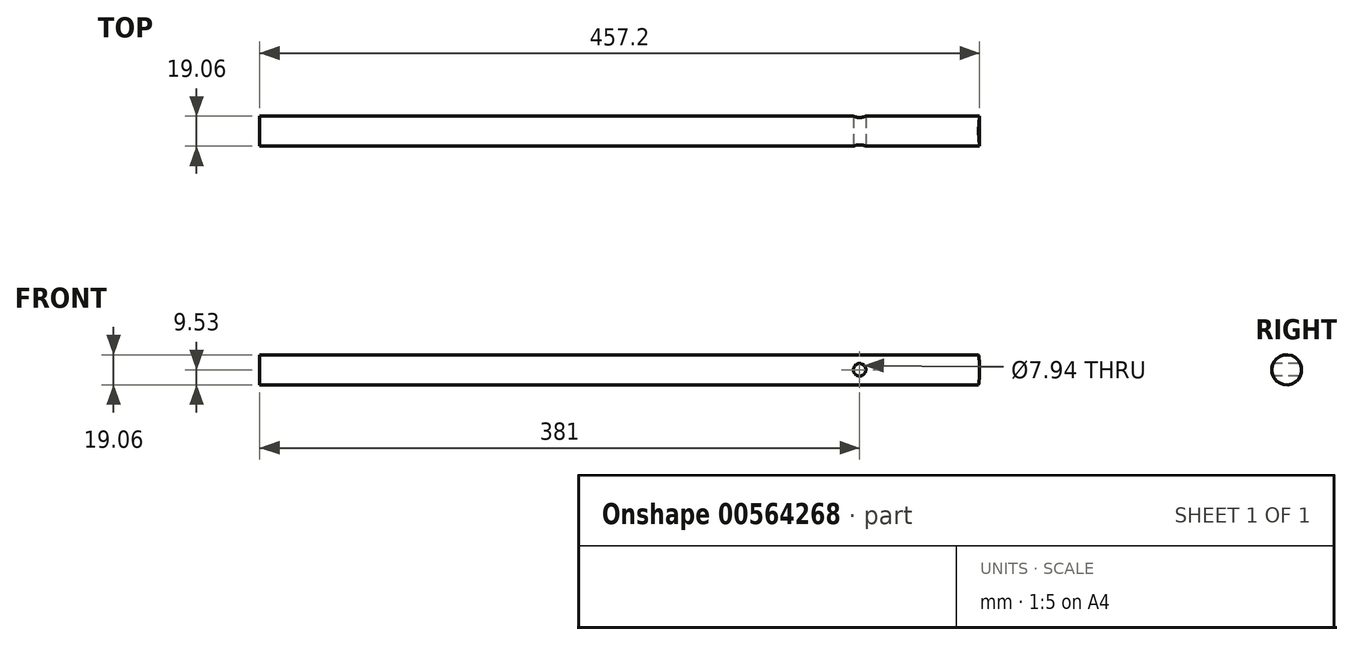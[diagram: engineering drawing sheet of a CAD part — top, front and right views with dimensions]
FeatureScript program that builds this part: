
annotation { "Feature Type Name" : "Feature", "Feature Type Description" : "" }
export const myFeature = defineFeature(function(context is Context, id is Id, definition is map)
    precondition{}
    {
        {
            var Q0;
            Q0=qCreatedBy(makeId("Right.planeOp"),FACE);
            var sketch = newSketch(context, id + "F0", { "sketchPlane" : qUnion([Q0])});
            skCircle(sketch, "E0", {"center": v(0, 0) * mm, "radius": 9.53 * mm});
            skSolve(sketch);
        }
        {
            var Q0;
            Q0=makeQuery(id+"F0.imprint","IMPRINT",FACE,{"disambiguationData":[TD([[makeQuery(id+"F0.imprint","IMPRINT",EDGE,{"derivedFrom":sQuery(id+"F0.wireOp",EDGE,"E0")}),1.0]])]});
            extrude(context, id + "F1", {"entities" : qUnion([Q0]), "endBound" : BoundingType.SYMMETRIC, "depth" : 457.2 * mm, "offsetDistance" : 25.4 * mm});
        }
        {
            var Q0;
            Q0=qCreatedBy(makeId("Front.planeOp"),FACE);
            var sketch = newSketch(context, id + "F2", { "sketchPlane" : qUnion([Q0])});
            skCircle(sketch, "E1", {"center": v(152.4, 0) * mm, "radius": 3.97 * mm});
            skArc(sketch, "E2", {"start": v(228, -9.52) * mm, "mid": v(228.6, 0) * mm, "end": v(228, 9.53) * mm});
            skLineSegment(sketch, "E3", {"start": v(228, 9.53) * mm, "end": v(235.25, 9.53) * mm});
            skLineSegment(sketch, "E4", {"start": v(235.25, 9.53) * mm, "end": v(235.25, -9.52) * mm});
            skLineSegment(sketch, "E5", {"start": v(235.25, -9.52) * mm, "end": v(228, -9.52) * mm});
            skSolve(sketch);
        }
        {
            var Q0;
            Q0 = qSketchRegion(id + "F2", true);
            extrude(context, id + "F3", {"entities" : qUnion([Q0]), "operationType" : NewBodyOperationType.REMOVE, "endBound" : BoundingType.SYMMETRIC, "oppositeDirection" : true, "depth" : 25.4 * mm, "offsetDistance" : 25.4 * mm});
        }
    });
